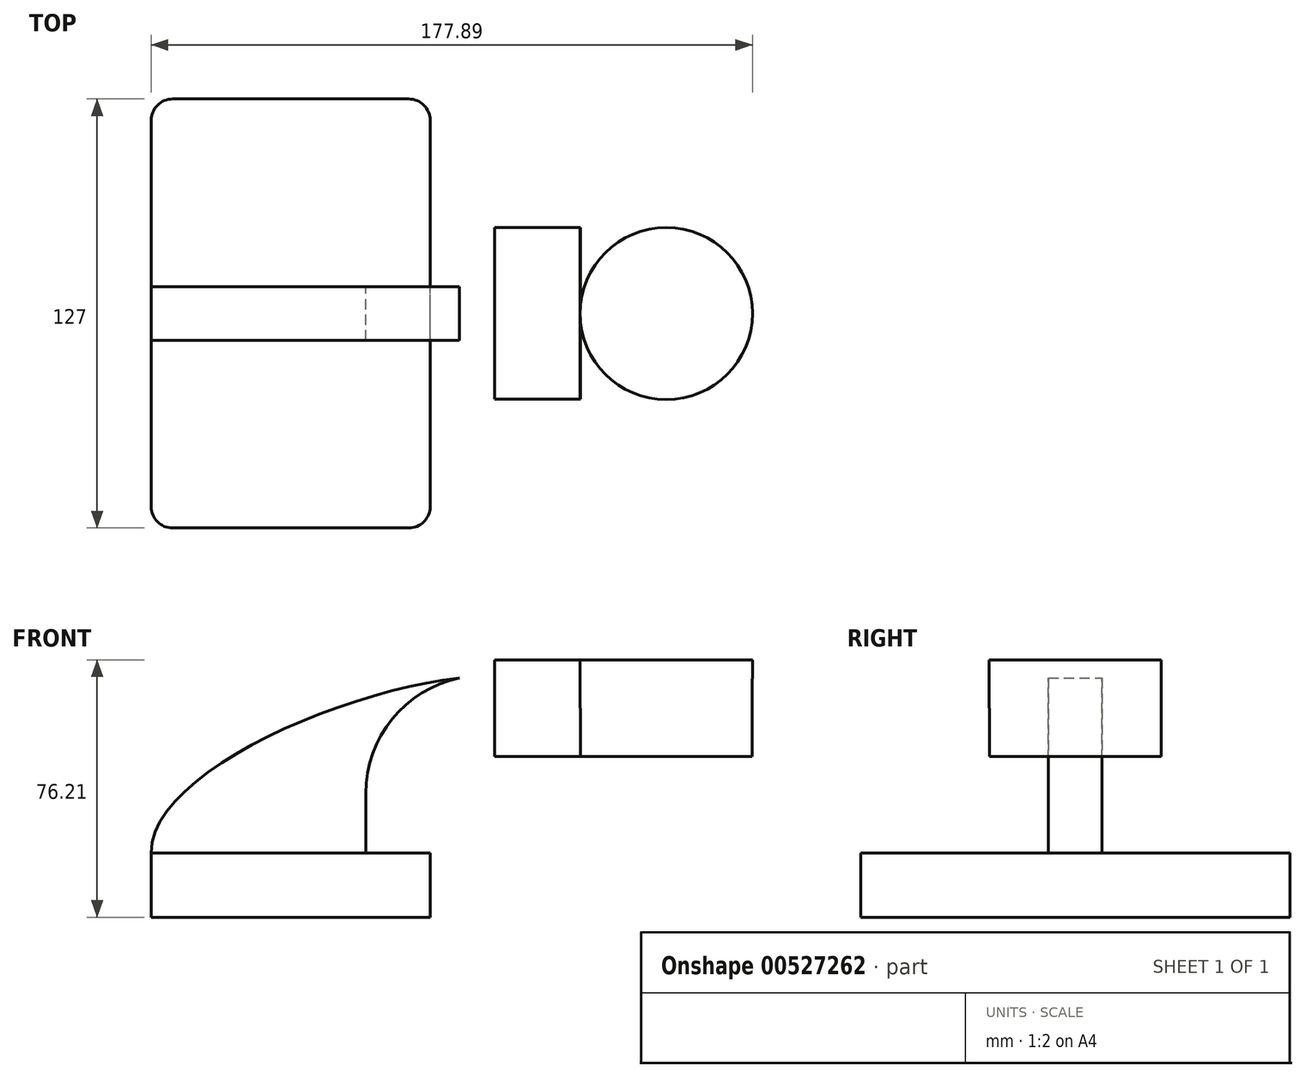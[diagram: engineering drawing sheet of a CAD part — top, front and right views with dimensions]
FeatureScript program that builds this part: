
annotation { "Feature Type Name" : "Feature", "Feature Type Description" : "" }
export const myFeature = defineFeature(function(context is Context, id is Id, definition is map)
    precondition{}
    {
        {
            var Q0;
            Q0=qCreatedBy(makeId("Front.planeOp"),FACE);
            var sketch = newSketch(context, id + "F0", { "sketchPlane" : qUnion([Q0])});
            skLineSegment(sketch, "E0.bottom", {"start": v(-41.28, -9.53) * mm, "end": v(41.28, -9.53) * mm});
            skLineSegment(sketch, "E0.top", {"start": v(-41.28, 9.53) * mm, "end": v(41.28, 9.53) * mm});
            skLineSegment(sketch, "E0.left", {"start": v(-41.28, -9.53) * mm, "end": v(-41.28, 9.53) * mm});
            skLineSegment(sketch, "E0.right", {"start": v(41.28, -9.53) * mm, "end": v(41.28, 9.53) * mm});
            skPoint(sketch, "E0.middle", {"position": v(0, 0) * mm});
            skLineSegment(sketch, "E1", {"start": v(41.28, 9.53) * mm, "end": v(41.28, 27.13) * mm});
            skArc(sketch, "E2", {"start": v(41.27, 27.13) * mm, "mid": v(45.25, 37.63) * mm, "end": v(55.19, 42.88) * mm});
            skLineSegment(sketch, "E3", {"start": v(55.19, 42.88) * mm, "end": v(85.72, 42.88) * mm});
            skLineSegment(sketch, "E4.bottom", {"start": v(60.33, 66.67) * mm, "end": v(111.13, 66.67) * mm});
            skLineSegment(sketch, "E4.top", {"start": v(60.33, 38.1) * mm, "end": v(111.13, 38.1) * mm});
            skLineSegment(sketch, "E4.left", {"start": v(60.33, 66.68) * mm, "end": v(60.33, 38.1) * mm});
            skLineSegment(sketch, "E4.right", {"start": v(111.13, 66.67) * mm, "end": v(111.13, 38.1) * mm});
            skPoint(sketch, "E4.middle", {"position": v(85.72, 52.39) * mm});
            skLineSegment(sketch, "E5.0", {"start": v(60.07, 61.93) * mm, "end": v(85.64, 61.93) * mm});
            skArc(sketch, "E5.1", {"start": v(22.22, 27.13) * mm, "mid": v(33.5, 52.83) * mm, "end": v(60.07, 61.93) * mm});
            skLineSegment(sketch, "E5.2", {"start": v(22.22, 9.53) * mm, "end": v(22.22, 27.13) * mm});
            skLineSegment(sketch, "E6", {"start": v(85.72, 38.1) * mm, "end": v(85.64, 66.67) * mm});
            skFitSpline(sketch, "E7", {"points": [v(-41.28, 9.53) * mm, v(60.07, 61.93) * mm], "startDerivative": vector(-0.53, 77.74) * mm, "endDerivative": vector(103.37, -0.04) * mm});
            skSolve(sketch);
        }
        {
            var Q0;
            Q0=makeQuery(id+"F0.imprint","IMPRINT",FACE,{"disambiguationData":[TD([[makeQuery(id+"F0.imprint","IMPRINT",EDGE,{"derivedFrom":sQuery(id+"F0.wireOp",EDGE,"E0.bottom")}),1.0]])]});
            extrude(context, id + "F1", {"entities" : qUnion([Q0]), "endBound" : BoundingType.SYMMETRIC, "depth" : 127 * mm, "offsetDistance" : 25.4 * mm});
        }
        {
            var Q0;
            {var subQ0=sQuery(id+"F0.wireOp",EDGE,"E2");Q0=makeQuery(id+"F0.imprint","IMPRINT",FACE,{"disambiguationData":[TD([[makeQuery(id+"F0.imprint","IMPRINT",EDGE,{"derivedFrom":subQ0}),1.0]])]});}
            var Q1;
            {var subQ1=sQuery(id+"F0.wireOp",EDGE,"E4.left");var subQ5=sQuery(id+"F0.wireOp",EDGE,"E4.bottom");var subQ6=makeQuery(id+"F0.imprint","INTERSECT",VERTEX,{"derivedFrom":[subQ5,subQ1]});Q1=makeQuery(id+"F0.imprint","IMPRINT",FACE,{"disambiguationData":[TD([[makeQuery(id+"F0.imprint","IMPRINT",EDGE,{"disambiguationData":[TD([[subQ6,-1.0]])],"derivedFrom":subQ5}),-1.0]])]});}
            var Q2;
            {var subQ0=sQuery(id+"F0.wireOp",EDGE,"E4.left");var subQ1=sQuery(id+"F0.wireOp",EDGE,"E4.top");var subQ2=makeQuery(id+"F0.imprint","INTERSECT",VERTEX,{"derivedFrom":[subQ1,subQ0]});Q2=makeQuery(id+"F0.imprint","IMPRINT",FACE,{"disambiguationData":[TD([[makeQuery(id+"F0.imprint","IMPRINT",EDGE,{"disambiguationData":[TD([[subQ2,-1.0]])],"derivedFrom":subQ1}),1.0]])]});}
            extrude(context, id + "F2", {"entities" : qUnion([Q0, Q1, Q2]), "operationType" : NewBodyOperationType.ADD, "endBound" : BoundingType.SYMMETRIC, "depth" : 50.8 * mm, "offsetDistance" : 25.4 * mm});
        }
        {
            var Q0;
            {var subQ3=sQuery(id+"F0.wireOp",EDGE,"E5.2");Q0=makeQuery(id+"F0.imprint","IMPRINT",FACE,{"disambiguationData":[TD([[makeQuery(id+"F0.imprint","IMPRINT",EDGE,{"derivedFrom":subQ3}),1.0]])]});}
            extrude(context, id + "F3", {"entities" : qUnion([Q0]), "operationType" : NewBodyOperationType.ADD, "endBound" : BoundingType.SYMMETRIC, "depth" : 15.88 * mm, "offsetDistance" : 25.4 * mm});
        }
        {
            var Q0;
            {var subQ0=sQuery(id+"F0.wireOp",EDGE,"E4.right");Q0=makeQuery(id+"F0.imprint","IMPRINT",FACE,{"disambiguationData":[TD([[makeQuery(id+"F0.imprint","IMPRINT",EDGE,{"derivedFrom":subQ0}),-1.0]])]});}
            var Q1;
            Q1=sQuery(id+"F0.wireOp",EDGE,"E6");
            var Q2;
            Q2=sQuery(id+"F0.wireOp",EDGE,"E4.right");
            revolve(context, id + "F4", {"entities" : qUnion([Q0]), "surfaceEntities" : qUnion([Q1]), "axis" : qUnion([Q2]), "revolveType" : RevolveType.FULL});
        }
        {
            var Q0;
            Q0=makeQuery(id+"F1.opExtrude","CAP_EDGE",EDGE,{"disambiguationData":[OSD([sQuery(id+"F0.wireOp",EDGE,"E0.right")])],"isStart":false});
            var Q1;
            Q1=makeQuery(id+"F1.opExtrude","CAP_EDGE",EDGE,{"disambiguationData":[OSD([sQuery(id+"F0.wireOp",EDGE,"E0.left")])],"isStart":false});
            var Q2;
            Q2=makeQuery(id+"F1.opExtrude","CAP_EDGE",EDGE,{"disambiguationData":[OSD([sQuery(id+"F0.wireOp",EDGE,"E0.left")])],"isStart":true});
            var Q3;
            Q3=makeQuery(id+"F1.opExtrude","CAP_EDGE",EDGE,{"disambiguationData":[OSD([sQuery(id+"F0.wireOp",EDGE,"E0.right")])],"isStart":true});
            fillet(context, id + "F5", {"entities" : qUnion([Q0, Q1, Q2, Q3]), "radius" : 6.35 * mm, "tangentPropagation" : true, "allowEdgeOverflow" : false});
        }
    });
